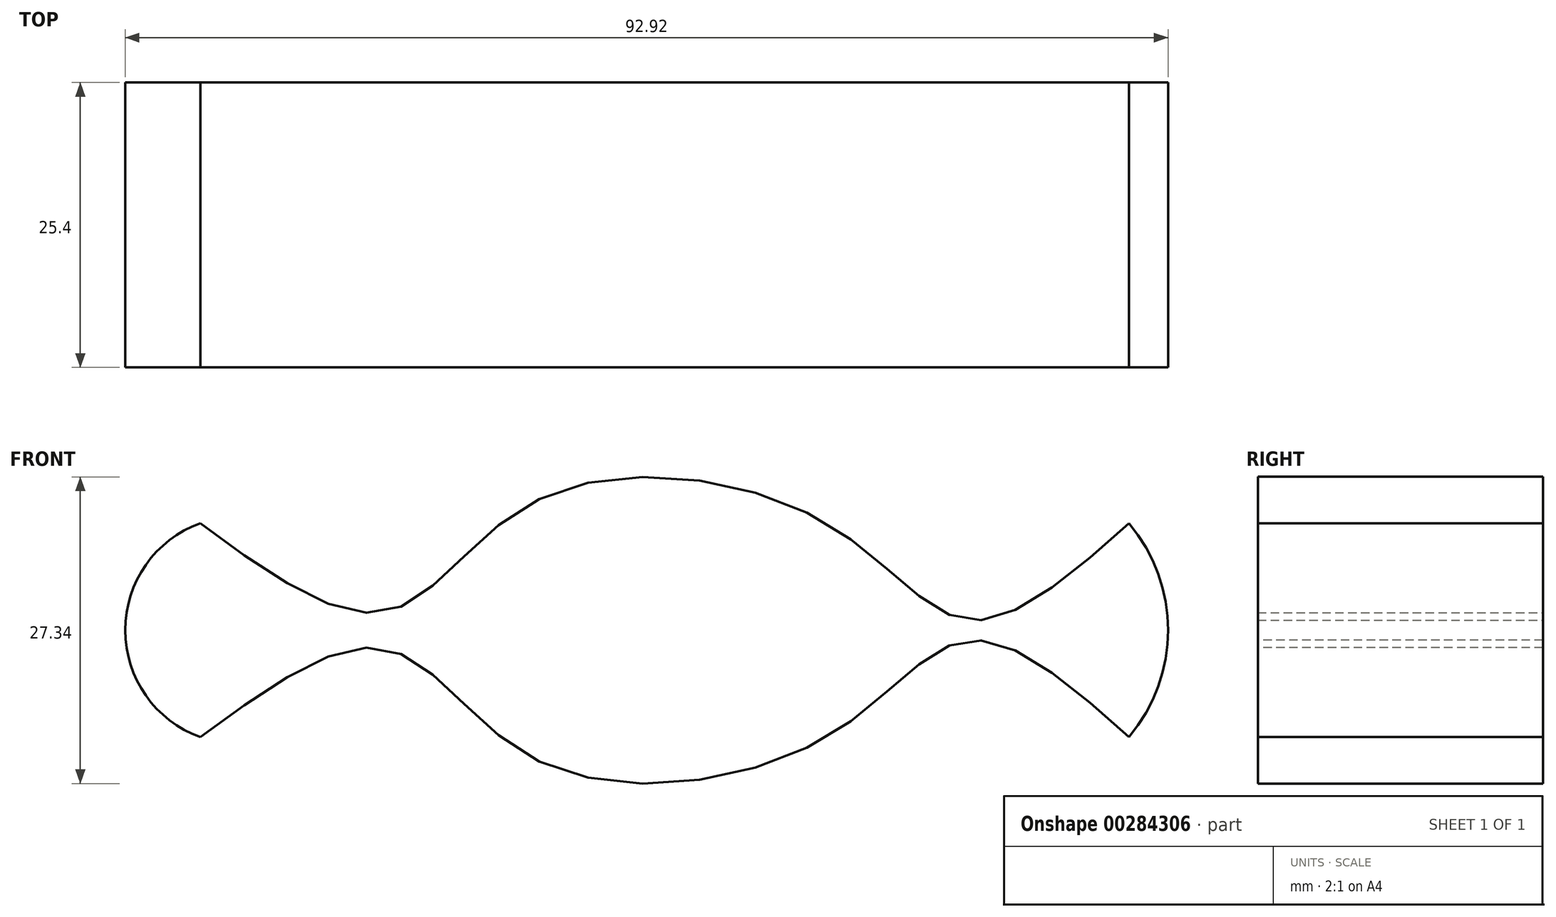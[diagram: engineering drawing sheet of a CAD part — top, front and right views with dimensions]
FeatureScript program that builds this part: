
annotation { "Feature Type Name" : "Feature", "Feature Type Description" : "" }
export const myFeature = defineFeature(function(context is Context, id is Id, definition is map)
    precondition{}
    {
        {
            var Q0;
            Q0=qCreatedBy(makeId("Front.planeOp"),FACE);
            var sketch = newSketch(context, id + "F0", { "sketchPlane" : qUnion([Q0])});
            skFitSpline(sketch, "E0", {"points": [v(40.76, 9.53) * mm, v(26.49, 0.9) * mm, v(13.82, 9.53) * mm, v(-11.79, 11.69) * mm, v(-25.27, 1.71) * mm, v(-41.98, 9.53) * mm], "startDerivative": vector(-79.77, -71.3) * mm, "endDerivative": vector(-90.28, 66.77) * mm});
            skFitSpline(sketch, "E1.MirrorCS", {"points": [v(40.76, -9.53) * mm, v(26.49, -0.9) * mm, v(13.82, -9.53) * mm, v(-11.79, -11.69) * mm, v(-25.27, -1.71) * mm, v(-41.98, -9.53) * mm], "startDerivative": vector(-79.77, 71.3) * mm, "endDerivative": vector(-90.28, -66.77) * mm});
            skArc(sketch, "E2", {"start": v(-41.98, 9.53) * mm, "mid": v(-48.67, 0) * mm, "end": v(-41.98, -9.53) * mm});
            skArc(sketch, "E3", {"start": v(40.76, -9.53) * mm, "mid": v(44.25, 0) * mm, "end": v(40.76, 9.53) * mm});
            skSolve(sketch);
        }
        {
            var Q0;
            Q0=makeQuery(id+"F0.imprint","IMPRINT",FACE,{"disambiguationData":[TD([[makeQuery(id+"F0.imprint","IMPRINT",EDGE,{"derivedFrom":sQuery(id+"F0.wireOp",EDGE,"E0")}),1.0]])]});
            extrude(context, id + "F1", {"entities" : qUnion([Q0]), "depth" : 25.4 * mm});
        }
    });
